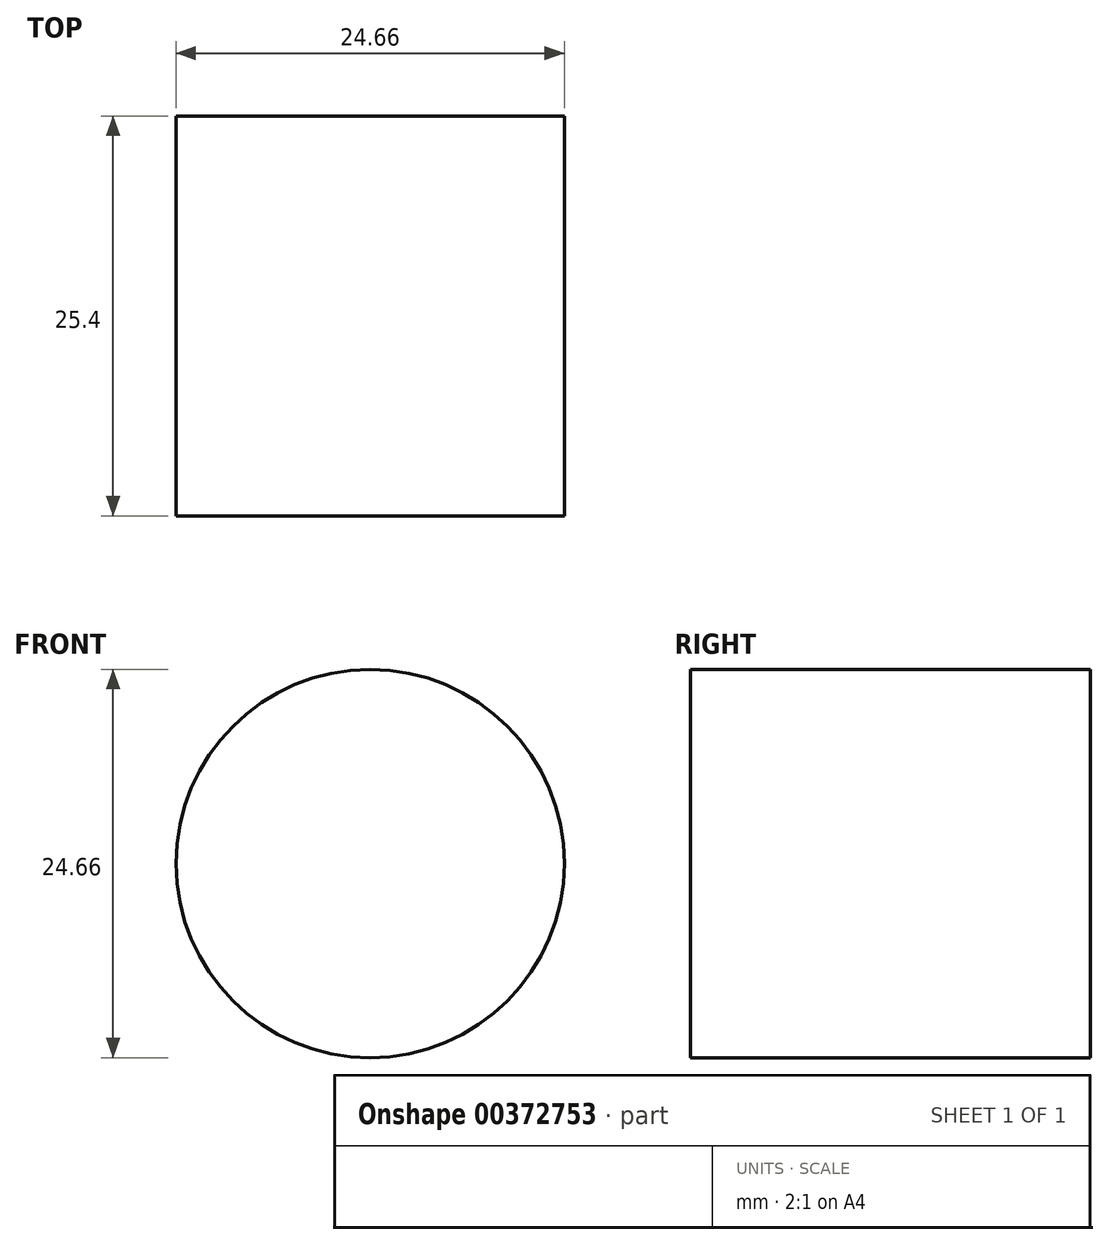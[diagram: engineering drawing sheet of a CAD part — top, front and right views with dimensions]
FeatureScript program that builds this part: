
annotation { "Feature Type Name" : "Feature", "Feature Type Description" : "" }
export const myFeature = defineFeature(function(context is Context, id is Id, definition is map)
    precondition{}
    {
        {
            var Q0;
            Q0=qCreatedBy(makeId("Front.planeOp"),FACE);
            var sketch = newSketch(context, id + "F0", { "sketchPlane" : qUnion([Q0])});
            skCircle(sketch, "E0", {"center": v(0, 0) * mm, "radius": 12.33 * mm});
            skSolve(sketch);
        }
        {
            var Q0;
            Q0=sQuery(id+"F0.wireOp",EDGE,"E0");
            extrude(context, id + "F1", {"bodyType" : ToolBodyType.SURFACE, "surfaceEntities" : qUnion([Q0]), "depth" : 25.4 * mm});
        }
    });
